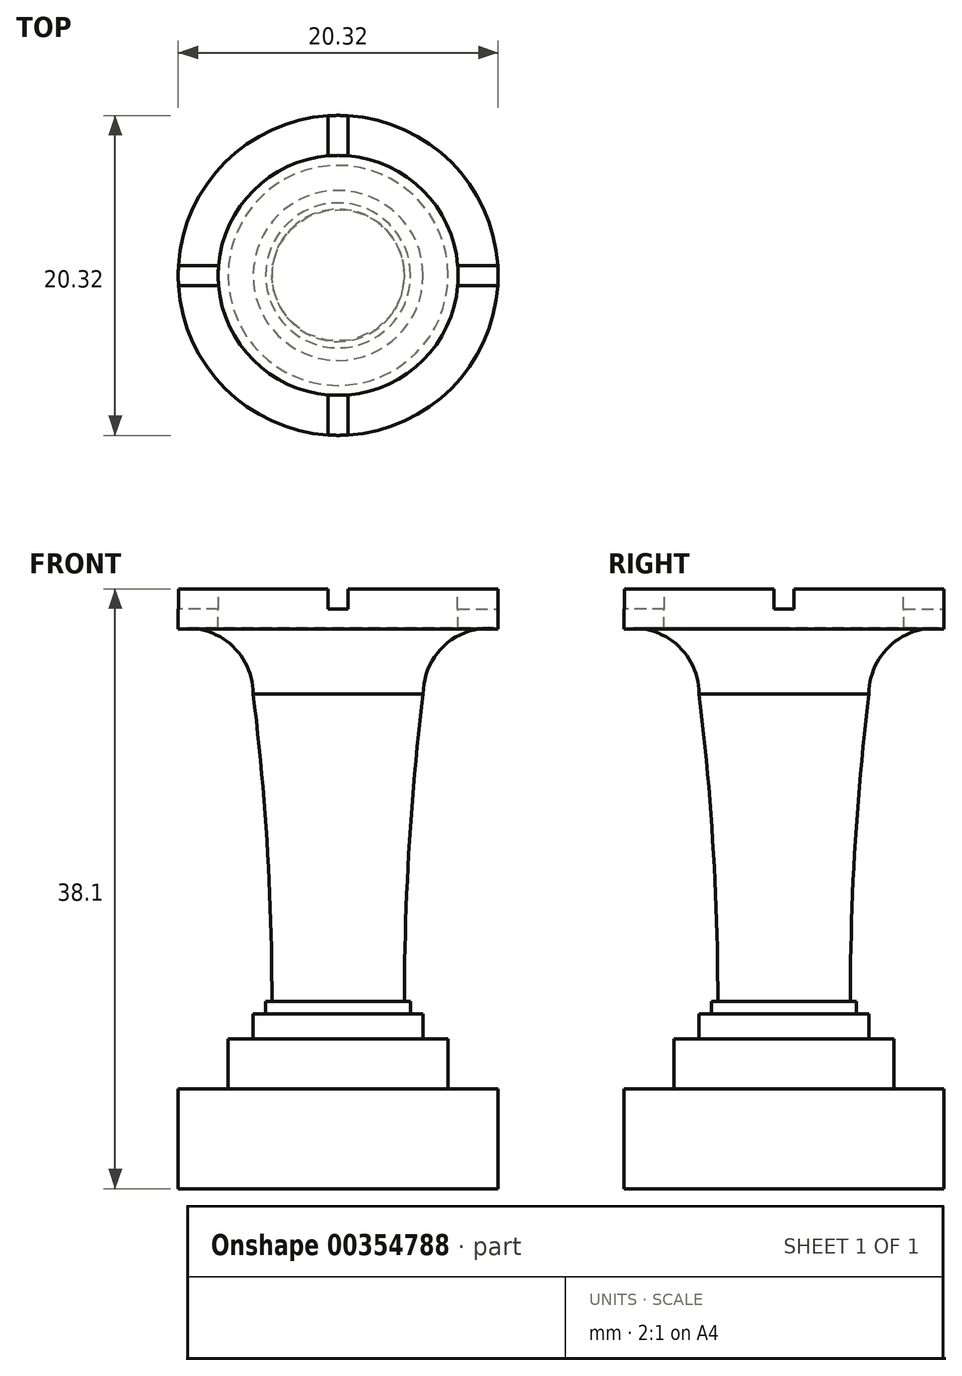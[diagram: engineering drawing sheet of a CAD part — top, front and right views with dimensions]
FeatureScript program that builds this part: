
annotation { "Feature Type Name" : "Feature", "Feature Type Description" : "" }
export const myFeature = defineFeature(function(context is Context, id is Id, definition is map)
    precondition{}
    {
        {
            var Q0;
            Q0=qCreatedBy(makeId("Front.planeOp"),FACE);
            var sketch = newSketch(context, id + "F0", { "sketchPlane" : qUnion([Q0])});
            skLineSegment(sketch, "E0", {"start": v(0, 0) * mm, "end": v(-10.16, 0) * mm});
            skLineSegment(sketch, "E1", {"start": v(-10.16, 0) * mm, "end": v(-10.16, 38.1) * mm, "construction": true});
            skLineSegment(sketch, "E2", {"start": v(0, 38.1) * mm, "end": v(-10.16, 38.1) * mm});
            skLineSegment(sketch, "E3", {"start": v(-10.16, 0) * mm, "end": v(-10.16, 6.35) * mm});
            skLineSegment(sketch, "E4", {"start": v(-10.16, 6.35) * mm, "end": v(-6.99, 6.35) * mm});
            skLineSegment(sketch, "E5", {"start": v(-6.99, 6.35) * mm, "end": v(-6.99, 9.53) * mm});
            skLineSegment(sketch, "E6", {"start": v(-6.99, 9.53) * mm, "end": v(-5.4, 9.53) * mm});
            skLineSegment(sketch, "E7", {"start": v(-5.4, 9.53) * mm, "end": v(-5.4, 11.11) * mm});
            skLineSegment(sketch, "E8", {"start": v(-5.4, 11.11) * mm, "end": v(-4.6, 11.11) * mm});
            skLineSegment(sketch, "E9", {"start": v(-4.6, 11.11) * mm, "end": v(-4.6, 11.9) * mm});
            skLineSegment(sketch, "E10", {"start": v(-4.6, 11.9) * mm, "end": v(-4.2, 11.9) * mm});
            skLineSegment(sketch, "E11", {"start": v(-5.4, 11.11) * mm, "end": v(-5.4, 31.43) * mm, "construction": true});
            skArc(sketch, "E12", {"start": v(-4.2, 11.9) * mm, "mid": v(-4.5, 21.69) * mm, "end": v(-5.4, 31.43) * mm});
            skLineSegment(sketch, "E13", {"start": v(-10.16, 38.1) * mm, "end": v(-10.16, 35.56) * mm});
            skArc(sketch, "E14", {"start": v(-5.4, 31.43) * mm, "mid": v(-6.84, 34.58) * mm, "end": v(-10.16, 35.56) * mm});
            skLineSegment(sketch, "E15", {"start": v(0, 38.1) * mm, "end": v(0, 0) * mm});
            skSolve(sketch);
        }
        {
            var Q0;
            Q0 = qSketchRegion(id + "F0", true);
            var Q1;
            Q1=sQuery(id+"F0.wireOp",EDGE,"E15");
            revolve(context, id + "F1", {"entities" : qUnion([Q0]), "axis" : qUnion([Q1]), "revolveType" : RevolveType.FULL});
        }
        {
            var Q0;
            Q0=makeQuery(id+"F1.opRevolve","SWEPT_FACE",FACE,{"disambiguationData":[OSD([sQuery(id+"F0.wireOp",EDGE,"E2")])]});
            var sketch = newSketch(context, id + "F2", { "sketchPlane" : qUnion([Q0])});
            skCircle(sketch, "E16", {"center": v(0, 0) * mm, "radius": 7.62 * mm});
            skLineSegment(sketch, "E17", {"start": v(0, 0.64) * mm, "end": v(0, 0) * mm, "construction": true});
            skLineSegment(sketch, "E18", {"start": v(-0.64, 0) * mm, "end": v(0, 0) * mm, "construction": true});
            skLineSegment(sketch, "E19", {"start": v(0, -0.64) * mm, "end": v(0, 0) * mm, "construction": true});
            skLineSegment(sketch, "E20", {"start": v(0.64, 0) * mm, "end": v(0, 0) * mm, "construction": true});
            skLineSegment(sketch, "E21", {"start": v(0, 0.64) * mm, "end": v(-10.16, 0.64) * mm});
            skLineSegment(sketch, "E22", {"start": v(-10.16, 0.63) * mm, "end": v(-10.16, -0.64) * mm});
            skLineSegment(sketch, "E23", {"start": v(-10.16, -0.64) * mm, "end": v(0, -0.64) * mm});
            skLineSegment(sketch, "E24", {"start": v(-0.64, 0) * mm, "end": v(-0.63, -10.16) * mm});
            skLineSegment(sketch, "E25", {"start": v(-0.63, -10.16) * mm, "end": v(0.64, -10.16) * mm});
            skLineSegment(sketch, "E26", {"start": v(0.64, -10.16) * mm, "end": v(0.64, 0) * mm});
            skLineSegment(sketch, "E27", {"start": v(0, 0.64) * mm, "end": v(10.16, 0.64) * mm});
            skLineSegment(sketch, "E28", {"start": v(10.16, 0.64) * mm, "end": v(10.16, -0.63) * mm});
            skLineSegment(sketch, "E29", {"start": v(10.16, -0.63) * mm, "end": v(0, -0.64) * mm});
            skLineSegment(sketch, "E30", {"start": v(-0.64, 0) * mm, "end": v(-0.64, 10.16) * mm});
            skLineSegment(sketch, "E31", {"start": v(-0.64, 10.16) * mm, "end": v(0.63, 10.16) * mm});
            skLineSegment(sketch, "E32", {"start": v(0.63, 10.16) * mm, "end": v(0.64, 0) * mm});
            skSolve(sketch);
        }
        {
            var Q0;
            {var subQ0=sQuery(id+"F2.wireOp",EDGE,"E26");var subQ1=sQuery(id+"F2.wireOp",EDGE,"E16");var subQ2=makeQuery(id+"F2.imprint","INTERSECT",VERTEX,{"derivedFrom":[subQ1,subQ0]});Q0=makeQuery(id+"F2.imprint","IMPRINT",FACE,{"disambiguationData":[TD([[makeQuery(id+"F2.imprint","IMPRINT",EDGE,{"disambiguationData":[TD([[subQ2,-1.0]])],"derivedFrom":subQ1}),1.0]])]});}
            var Q1;
            {var subQ1=sQuery(id+"F2.wireOp",EDGE,"E16");var subQ7=sQuery(id+"F2.wireOp",EDGE,"E24");var subQ8=makeQuery(id+"F2.imprint","INTERSECT",VERTEX,{"derivedFrom":[subQ1,subQ7]});Q1=makeQuery(id+"F2.imprint","IMPRINT",FACE,{"disambiguationData":[TD([[makeQuery(id+"F2.imprint","IMPRINT",EDGE,{"disambiguationData":[TD([[subQ8,-1.0]])],"derivedFrom":subQ1}),1.0]])]});}
            var Q2;
            {var subQ0=sQuery(id+"F2.wireOp",EDGE,"E23");var subQ1=sQuery(id+"F2.wireOp",EDGE,"E16");var subQ2=makeQuery(id+"F2.imprint","INTERSECT",VERTEX,{"derivedFrom":[subQ1,subQ0]});Q2=makeQuery(id+"F2.imprint","IMPRINT",FACE,{"disambiguationData":[TD([[makeQuery(id+"F2.imprint","IMPRINT",EDGE,{"disambiguationData":[TD([[subQ2,-1.0]])],"derivedFrom":subQ1}),1.0]])]});}
            var Q3;
            {var subQ1=sQuery(id+"F2.wireOp",EDGE,"E16");var subQ7=sQuery(id+"F2.wireOp",EDGE,"E21");var subQ9=makeQuery(id+"F2.imprint","INTERSECT",VERTEX,{"derivedFrom":[subQ1,subQ7]});Q3=makeQuery(id+"F2.imprint","IMPRINT",FACE,{"disambiguationData":[TD([[makeQuery(id+"F2.imprint","IMPRINT",EDGE,{"disambiguationData":[TD([[subQ9,-1.0]])],"derivedFrom":subQ1}),1.0]])]});}
            var Q4;
            {var subQ0=sQuery(id+"F2.wireOp",EDGE,"E30");var subQ1=sQuery(id+"F2.wireOp",EDGE,"E16");var subQ2=makeQuery(id+"F2.imprint","INTERSECT",VERTEX,{"derivedFrom":[subQ1,subQ0]});Q4=makeQuery(id+"F2.imprint","IMPRINT",FACE,{"disambiguationData":[TD([[makeQuery(id+"F2.imprint","IMPRINT",EDGE,{"disambiguationData":[TD([[subQ2,-1.0]])],"derivedFrom":subQ1}),1.0]])]});}
            var Q5;
            {var subQ1=sQuery(id+"F2.wireOp",EDGE,"E16");var subQ7=sQuery(id+"F2.wireOp",EDGE,"E32");var subQ9=makeQuery(id+"F2.imprint","INTERSECT",VERTEX,{"derivedFrom":[subQ1,subQ7]});Q5=makeQuery(id+"F2.imprint","IMPRINT",FACE,{"disambiguationData":[TD([[makeQuery(id+"F2.imprint","IMPRINT",EDGE,{"disambiguationData":[TD([[subQ9,-1.0]])],"derivedFrom":subQ1}),1.0]])]});}
            var Q6;
            {var subQ0=sQuery(id+"F2.wireOp",EDGE,"E32");var subQ1=sQuery(id+"F2.wireOp",EDGE,"E16");var subQ2=makeQuery(id+"F2.imprint","INTERSECT",VERTEX,{"derivedFrom":[subQ1,subQ0]});Q6=makeQuery(id+"F2.imprint","IMPRINT",FACE,{"disambiguationData":[TD([[makeQuery(id+"F2.imprint","IMPRINT",EDGE,{"disambiguationData":[TD([[subQ2,1.0]])],"derivedFrom":subQ1}),1.0]])]});}
            var Q7;
            {var subQ8=sQuery(id+"F2.wireOp",EDGE,"E21");var subQ13=sQuery(id+"F2.wireOp",EDGE,"E27");var subQ14=makeQuery(id+"F2.imprint","INTERSECT",VERTEX,{"derivedFrom":[subQ8,subQ13]});Q7=makeQuery(id+"F2.imprint","IMPRINT",FACE,{"disambiguationData":[TD([[makeQuery(id+"F2.imprint","IMPRINT",EDGE,{"disambiguationData":[TD([[subQ14,-1.0]])],"derivedFrom":subQ8}),1.0]])]});}
            var Q8;
            {var subQ1=sQuery(id+"F2.wireOp",EDGE,"E16");var subQ7=sQuery(id+"F2.wireOp",EDGE,"E27");var subQ9=makeQuery(id+"F2.imprint","INTERSECT",VERTEX,{"derivedFrom":[subQ1,subQ7]});Q8=makeQuery(id+"F2.imprint","IMPRINT",FACE,{"disambiguationData":[TD([[makeQuery(id+"F2.imprint","IMPRINT",EDGE,{"disambiguationData":[TD([[subQ9,1.0]])],"derivedFrom":subQ1}),1.0]])]});}
            extrude(context, id + "F3", {"entities" : qUnion([Q0, Q1, Q2, Q3, Q4, Q5, Q6, Q7, Q8]), "operationType" : NewBodyOperationType.REMOVE, "oppositeDirection" : true, "depth" : 2.54 * mm});
        }
        {
            var Q0;
            {var subQ0=sQuery(id+"F2.wireOp",EDGE,"E21");var subQ5=sQuery(id+"F2.wireOp",EDGE,"E16");var subQ8=makeQuery(id+"F2.imprint","INTERSECT",VERTEX,{"derivedFrom":[subQ5,subQ0]});Q0=makeQuery(id+"F2.imprint","IMPRINT",FACE,{"disambiguationData":[TD([[makeQuery(id+"F2.imprint","IMPRINT",EDGE,{"disambiguationData":[TD([[subQ8,-1.0]])],"derivedFrom":subQ5}),-1.0]])]});}
            var Q1;
            {var subQ4=sQuery(id+"F2.wireOp",EDGE,"E32");var subQ5=sQuery(id+"F2.wireOp",EDGE,"E16");var subQ6=makeQuery(id+"F2.imprint","INTERSECT",VERTEX,{"derivedFrom":[subQ5,subQ4]});Q1=makeQuery(id+"F2.imprint","IMPRINT",FACE,{"disambiguationData":[TD([[makeQuery(id+"F2.imprint","IMPRINT",EDGE,{"disambiguationData":[TD([[subQ6,-1.0]])],"derivedFrom":subQ5}),-1.0]])]});}
            var Q2;
            {var subQ0=sQuery(id+"F2.wireOp",EDGE,"E27");var subQ5=sQuery(id+"F2.wireOp",EDGE,"E16");var subQ8=makeQuery(id+"F2.imprint","INTERSECT",VERTEX,{"derivedFrom":[subQ5,subQ0]});Q2=makeQuery(id+"F2.imprint","IMPRINT",FACE,{"disambiguationData":[TD([[makeQuery(id+"F2.imprint","IMPRINT",EDGE,{"disambiguationData":[TD([[subQ8,1.0]])],"derivedFrom":subQ5}),-1.0]])]});}
            var Q3;
            {var subQ0=sQuery(id+"F2.wireOp",EDGE,"E24");var subQ5=sQuery(id+"F2.wireOp",EDGE,"E16");var subQ8=makeQuery(id+"F2.imprint","INTERSECT",VERTEX,{"derivedFrom":[subQ5,subQ0]});Q3=makeQuery(id+"F2.imprint","IMPRINT",FACE,{"disambiguationData":[TD([[makeQuery(id+"F2.imprint","IMPRINT",EDGE,{"disambiguationData":[TD([[subQ8,-1.0]])],"derivedFrom":subQ5}),-1.0]])]});}
            extrude(context, id + "F4", {"entities" : qUnion([Q0, Q1, Q2, Q3]), "operationType" : NewBodyOperationType.REMOVE, "oppositeDirection" : true, "depth" : 1.27 * mm});
        }
    });
